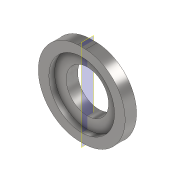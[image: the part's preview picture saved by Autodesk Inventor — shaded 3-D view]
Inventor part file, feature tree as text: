
AUTODESK INVENTOR PART (.ipt)
format: ipt  version: 2020.3 (Build 243373010, 373A)  size: 118,272 bytes
history: native  units: mm
features: extrude x2, sketch x2, plane x1
ambient origin geometry x8: Origin, YZ Plane, XZ Plane, XY Plane, X Axis, Y Axis, Z Axis, Center Point
bodies: Solid1 (feature_tree)
feature tree (5):
  extrude  "Extrusion1"  Depth=36.25mm
  extrude  "Extrusion2"  Depth=10.0mm TaperAngle=0.0deg
  plane  "Work Plane1"
  sketch  "Sketch1"  dims[d0=57.5mm d1=36.25mm]
  sketch  "Sketch2"  dims[d2=36.25mm d3=10.0mm d4=0.0mm d5=37.125mm d6=10.0mm d7=0.0mm d8=7.054879mm]
